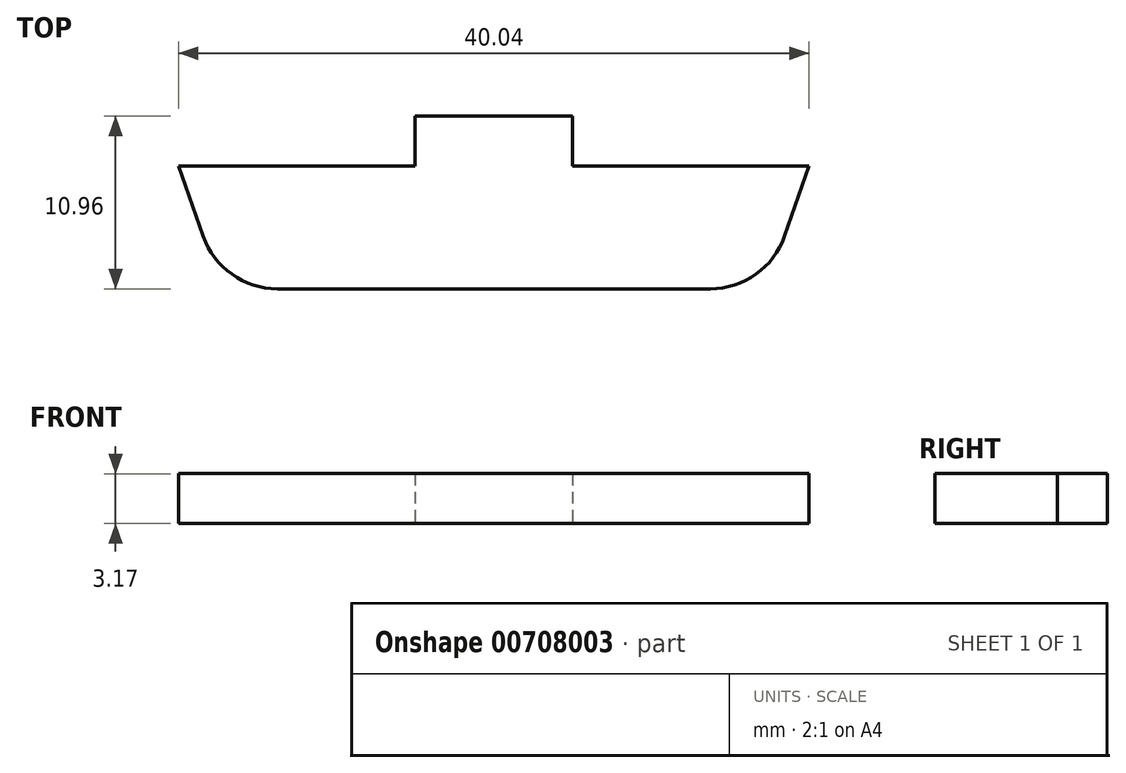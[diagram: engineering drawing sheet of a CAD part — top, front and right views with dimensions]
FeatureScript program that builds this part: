
annotation { "Feature Type Name" : "Feature", "Feature Type Description" : "" }
export const myFeature = defineFeature(function(context is Context, id is Id, definition is map)
    precondition{}
    {
        {
            var Q0;
            Q0=qCreatedBy(makeId("Top.planeOp"), FACE);
            var sketch = newSketch(context, id + "F0", { "sketchPlane" : qUnion([Q0])});
            skPoint(sketch, "E0.0", {"position": v(-23.57, 45.02) * mm});
            skPoint(sketch, "E1.0", {"position": v(16.47, 45.02) * mm});
            skLineSegment(sketch, "E2.0", {"start": v(1.45, -2.33) * mm, "end": v(16.47, -2.33) * mm});
            skPoint(sketch, "E3.0", {"position": v(1.45, -0.75) * mm});
            skLineSegment(sketch, "E4.0", {"start": v(1.45, 0.84) * mm, "end": v(1.45, -2.33) * mm});
            skLineSegment(sketch, "E5.0", {"start": v(-3.55, 0.84) * mm, "end": v(1.45, 0.84) * mm});
            skLineSegment(sketch, "E6.0", {"start": v(-3.55, 0.84) * mm, "end": v(-8.55, 0.84) * mm});
            skLineSegment(sketch, "E7.0", {"start": v(-8.55, 0.84) * mm, "end": v(-8.55, -2.33) * mm});
            skLineSegment(sketch, "E8.0", {"start": v(-23.57, -2.33) * mm, "end": v(-8.55, -2.33) * mm});
            skLineSegment(sketch, "E9", {"start": v(16.47, 45.02) * mm, "end": v(16.47, -2.33) * mm, "construction": true});
            skLineSegment(sketch, "E10", {"start": v(-23.57, 45.02) * mm, "end": v(-23.57, -2.33) * mm, "construction": true});
            skPoint(sketch, "E11.0", {"position": v(16.98, -6.23) * mm});
            skLineSegment(sketch, "E12", {"start": v(16.47, -2.33) * mm, "end": v(14.92, -6.77) * mm});
            skLineSegment(sketch, "E13", {"start": v(-3.55, 0.84) * mm, "end": v(-3.55, -12.18) * mm, "construction": true});
            skLineSegment(sketch, "E14.MirrorCS", {"start": v(-23.57, -2.33) * mm, "end": v(-22.01, -6.77) * mm});
            skLineSegment(sketch, "E15", {"start": v(10.2, -10.12) * mm, "end": v(-17.3, -10.12) * mm});
            skPoint(sketch, "E16.orphan", {"position": v(15.62, -10.12) * mm});
            skPoint(sketch, "E17.visualSharp", {"position": v(13.75, -10.12) * mm});
            skArc(sketch, "E17.filletArc", {"start": v(10.2, -10.12) * mm, "mid": v(13.1, -9.2) * mm, "end": v(14.92, -6.77) * mm});
            skPoint(sketch, "E18.visualSharp", {"position": v(-20.84, -10.12) * mm});
            skArc(sketch, "E18.filletArc", {"start": v(-22.01, -6.77) * mm, "mid": v(-20.19, -9.2) * mm, "end": v(-17.3, -10.12) * mm});
            skPoint(sketch, "E19.0.start.orphan", {"position": v(18.35, -2.33) * mm});
            skPoint(sketch, "E20.trimOffspring.end.orphan", {"position": v(29.33, -2.33) * mm});
            skPoint(sketch, "E21.orphan", {"position": v(-36.42, -2.33) * mm});
            skSolve(sketch);
        }
        {
            var Q0;
            Q0 = qSketchRegion(id + "F0", true);
            extrude(context, id + "F1", {"entities" : qUnion([Q0]), "depth" : 3.17 * mm, "offsetDistance" : 25 * mm});
        }
    });
